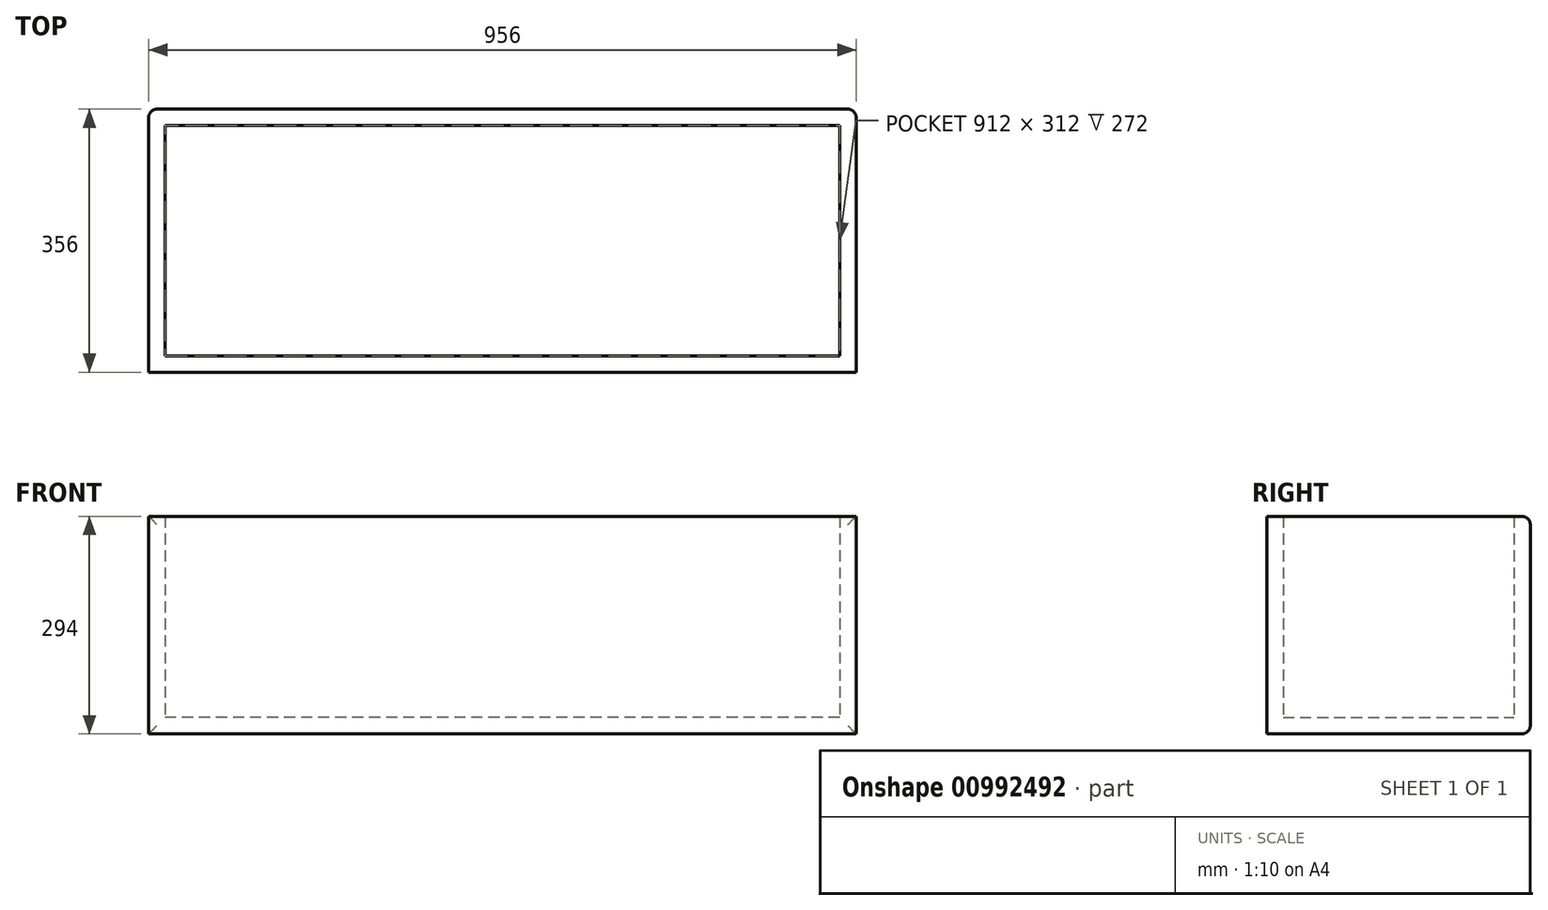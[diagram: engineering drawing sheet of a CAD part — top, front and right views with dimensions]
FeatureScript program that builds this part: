
annotation { "Feature Type Name" : "Feature", "Feature Type Description" : "" }
export const myFeature = defineFeature(function(context is Context, id is Id, definition is map)
    precondition{}
    {
        {
            var Q0;
            Q0=qCreatedBy(makeId("Top.planeOp"),FACE);
            var sketch = newSketch(context, id + "F0", { "sketchPlane" : qUnion([Q0])});
            skLineSegment(sketch, "E0.bottom", {"start": v(478, -178) * mm, "end": v(-478, -178) * mm});
            skLineSegment(sketch, "E0.top", {"start": v(478, 178) * mm, "end": v(-478, 178) * mm});
            skLineSegment(sketch, "E0.left", {"start": v(478, -178) * mm, "end": v(478, 178) * mm});
            skLineSegment(sketch, "E0.right", {"start": v(-478, -178) * mm, "end": v(-478, 178) * mm});
            skPoint(sketch, "E0.middle", {"position": v(0, 0) * mm});
            skSolve(sketch);
        }
        {
            var Q0;
            Q0=makeQuery(id+"F0.imprint","IMPRINT",FACE,{"disambiguationData":[TD([[makeQuery(id+"F0.imprint","IMPRINT",EDGE,{"derivedFrom":sQuery(id+"F0.wireOp",EDGE,"E0.bottom")}),-1.0]])]});
            extrude(context, id + "F1", {"entities" : qUnion([Q0]), "depth" : 294 * mm, "offsetDistance" : 25 * mm});
        }
        {
            var Q0;
            Q0=makeQuery(id+"F1.opExtrude","CAP_FACE",FACE,{"disambiguationData":[OSD([sQuery(id+"F0.wireOp",EDGE,"E0.bottom"),sQuery(id+"F0.wireOp",EDGE,"E0.top"),sQuery(id+"F0.wireOp",EDGE,"E0.left"),sQuery(id+"F0.wireOp",EDGE,"E0.right")])],"isStart":false});
            shell(context, id + "F2", {"entities" : qUnion([Q0]), "thickness" : 22 * mm});
        }
        {
            var Q0;
            Q0=makeQuery(id+"F1.opExtrude","SWEPT_FACE",FACE,{"disambiguationData":[OSD([sQuery(id+"F0.wireOp",EDGE,"E0.top")])]});
            fillet(context, id + "F3", {"entities" : qUnion([Q0]), "radius" : 11 * mm, "tangentPropagation" : true, "allowEdgeOverflow" : false});
        }
    });
